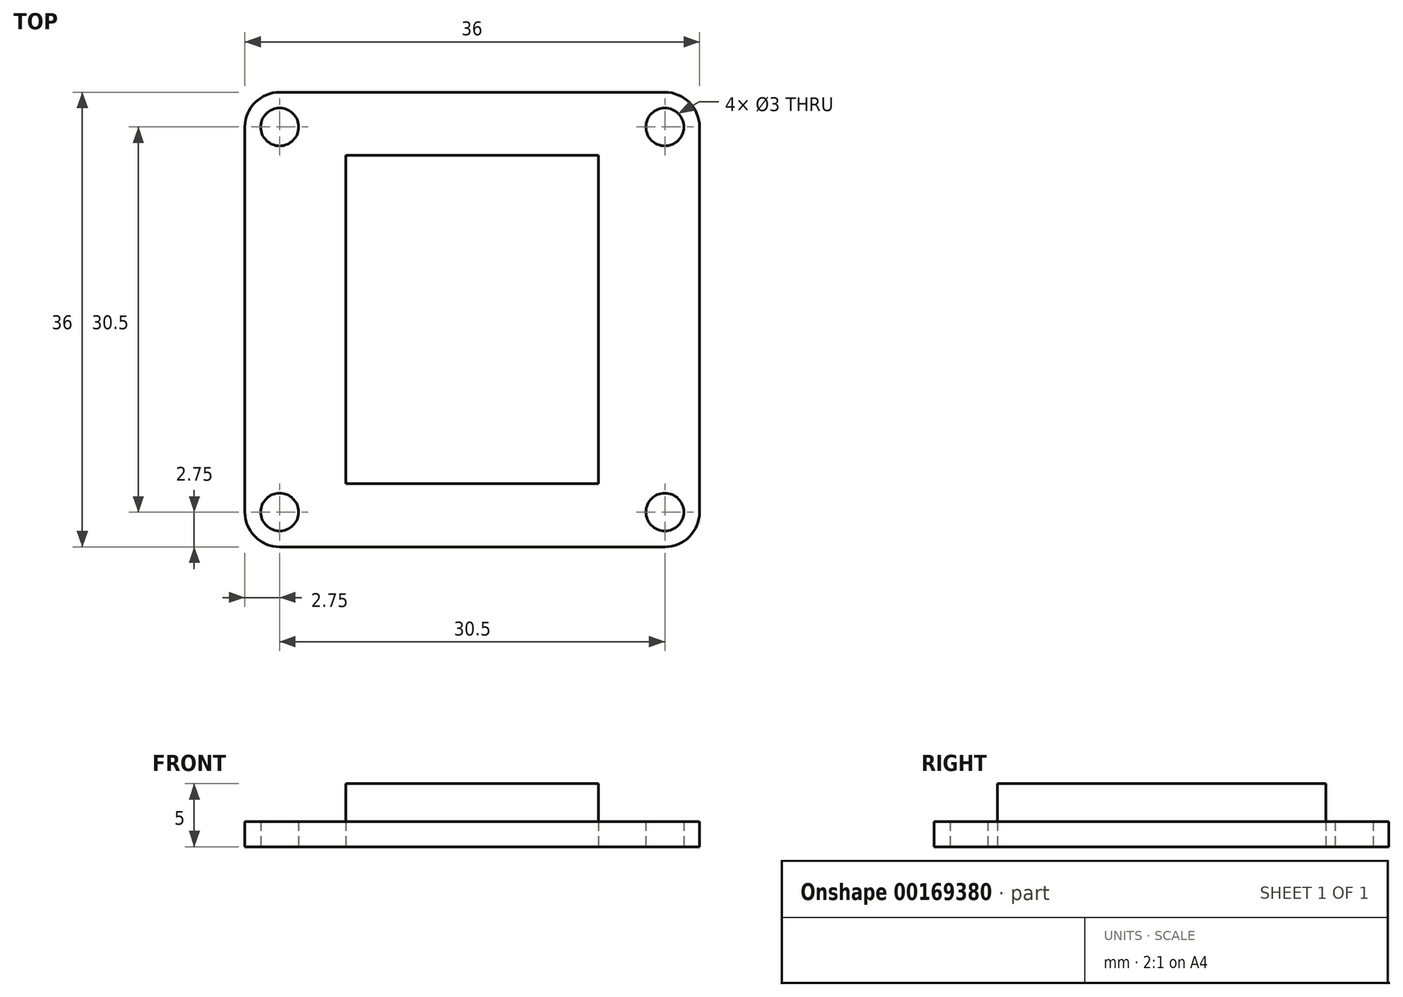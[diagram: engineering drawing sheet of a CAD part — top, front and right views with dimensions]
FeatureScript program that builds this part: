
annotation { "Feature Type Name" : "Feature", "Feature Type Description" : "" }
export const myFeature = defineFeature(function(context is Context, id is Id, definition is map)
    precondition{}
    {
        {
            var Q0;
            Q0=qCreatedBy(makeId("Top.planeOp"),FACE);
            var sketch = newSketch(context, id + "F0", { "sketchPlane" : qUnion([Q0])});
            skLineSegment(sketch, "E0.bottom", {"start": v(-15.25, 18) * mm, "end": v(15.25, 18) * mm});
            skLineSegment(sketch, "E0.top", {"start": v(-15.25, -18) * mm, "end": v(15.25, -18) * mm});
            skLineSegment(sketch, "E0.left", {"start": v(-18, 15.25) * mm, "end": v(-18, -15.25) * mm});
            skLineSegment(sketch, "E0.right", {"start": v(18, 15.25) * mm, "end": v(18, -15.25) * mm});
            skCircle(sketch, "E1", {"center": v(-15.25, 15.25) * mm, "radius": 1.5 * mm});
            skCircle(sketch, "E2.0.1.0", {"center": v(-15.25, -15.25) * mm, "radius": 1.5 * mm});
            skCircle(sketch, "E2.1.0.0", {"center": v(15.25, 15.25) * mm, "radius": 1.5 * mm});
            skCircle(sketch, "E2.1.1.0", {"center": v(15.25, -15.25) * mm, "radius": 1.5 * mm});
            skLineSegment(sketch, "E2.direction1", {"start": v(-15.25, 15.25) * mm, "end": v(15.25, 15.25) * mm, "construction": true});
            skLineSegment(sketch, "E2.direction2", {"start": v(-15.25, 15.25) * mm, "end": v(-15.25, -15.25) * mm, "construction": true});
            skPoint(sketch, "E3.visualSharp", {"position": v(-18, 18) * mm});
            skArc(sketch, "E3.filletArc", {"start": v(-15.25, 18) * mm, "mid": v(-17.2, 17.2) * mm, "end": v(-18, 15.25) * mm});
            skPoint(sketch, "E4.visualSharp", {"position": v(18, 18) * mm});
            skArc(sketch, "E4.filletArc", {"start": v(18, 15.25) * mm, "mid": v(17.2, 17.2) * mm, "end": v(15.25, 18) * mm});
            skPoint(sketch, "E5.visualSharp", {"position": v(18, -18) * mm});
            skArc(sketch, "E5.filletArc", {"start": v(15.25, -18) * mm, "mid": v(17.2, -17.2) * mm, "end": v(18, -15.25) * mm});
            skPoint(sketch, "E6.visualSharp", {"position": v(-18, -18) * mm});
            skArc(sketch, "E6.filletArc", {"start": v(-18, -15.25) * mm, "mid": v(-17.2, -17.2) * mm, "end": v(-15.25, -18) * mm});
            skSolve(sketch);
        }
        {
            var Q0;
            Q0=makeQuery(id+"F0.imprint","IMPRINT",FACE,{"disambiguationData":[TD([[makeQuery(id+"F0.imprint","IMPRINT",EDGE,{"derivedFrom":sQuery(id+"F0.wireOp",EDGE,"E0.bottom")}),-1.0]])]});
            extrude(context, id + "F1", {"entities" : qUnion([Q0]), "depth" : 2 * mm});
        }
        {
            var Q0;
            Q0=qCreatedBy(makeId("Top.planeOp"),FACE);
            var sketch = newSketch(context, id + "F2", { "sketchPlane" : qUnion([Q0])});
            skLineSegment(sketch, "E7.bottom", {"start": v(-10, 13) * mm, "end": v(10, 13) * mm});
            skLineSegment(sketch, "E7.top", {"start": v(-10, -13) * mm, "end": v(10, -13) * mm});
            skLineSegment(sketch, "E7.left", {"start": v(-10, 13) * mm, "end": v(-10, -13) * mm});
            skLineSegment(sketch, "E7.right", {"start": v(10, 13) * mm, "end": v(10, -13) * mm});
            skSolve(sketch);
        }
        {
            var Q0;
            Q0=qSketchRegion(id+"F2",true);
            extrude(context, id + "F3", {"entities" : qUnion([Q0]), "depth" : 5 * mm});
        }
    });
